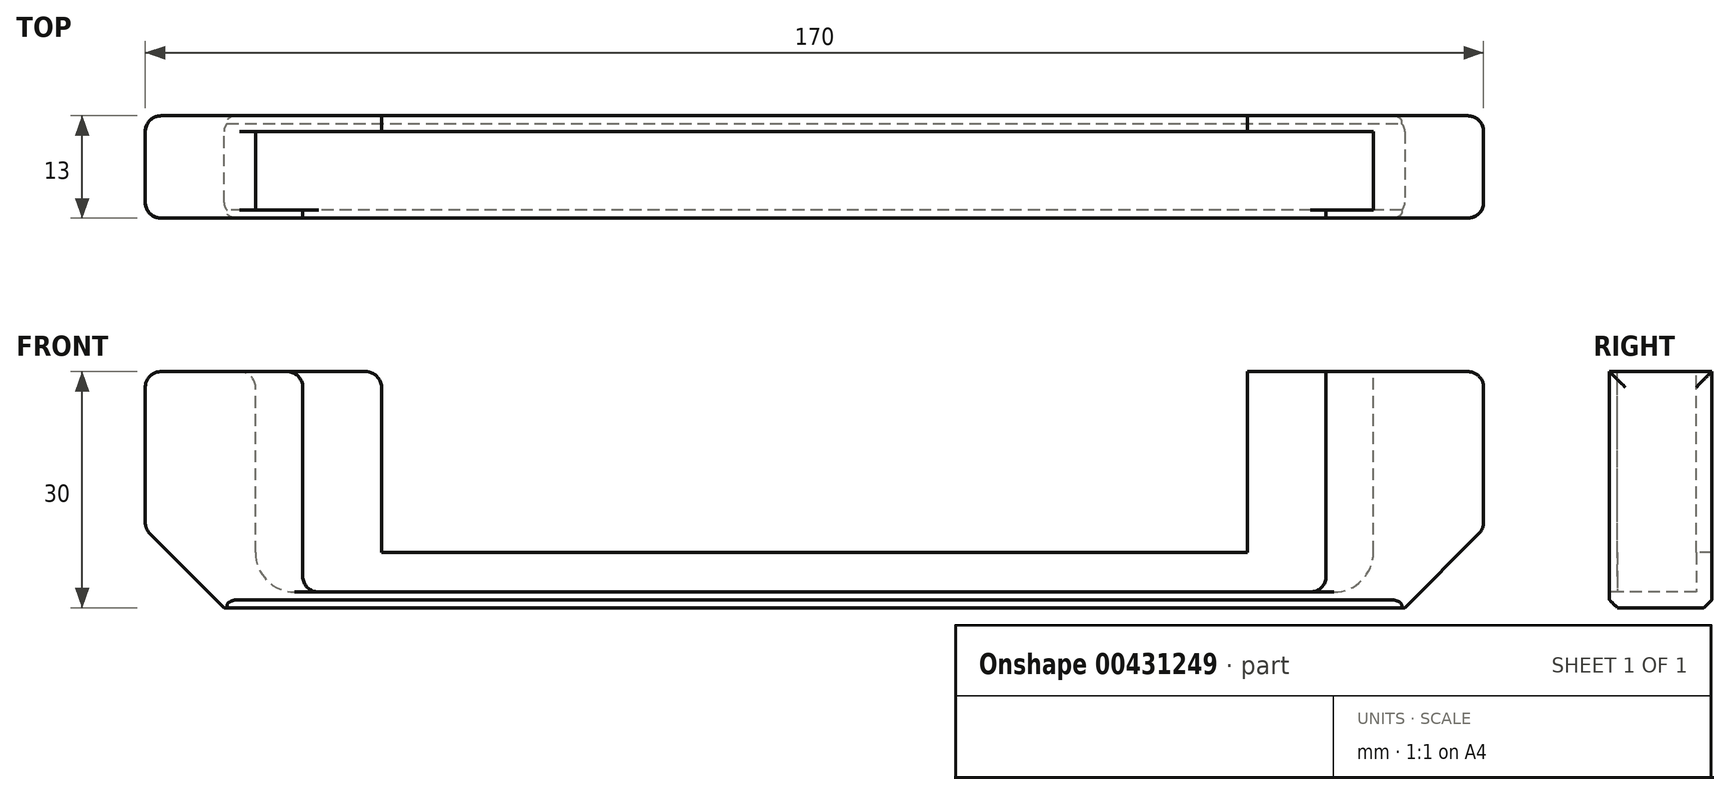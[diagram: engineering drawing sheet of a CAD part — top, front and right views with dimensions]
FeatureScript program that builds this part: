
annotation { "Feature Type Name" : "Feature", "Feature Type Description" : "" }
export const myFeature = defineFeature(function(context is Context, id is Id, definition is map)
    precondition{}
    {
        {
            var Q0;
            Q0=qCreatedBy(makeId("Front.planeOp"),FACE);
            var sketch = newSketch(context, id + "F0", { "sketchPlane" : qUnion([Q0])});
            skLineSegment(sketch, "E0.bottom", {"start": v(-85, 0) * mm, "end": v(85, 0) * mm});
            skLineSegment(sketch, "E0.top", {"start": v(-85, 30) * mm, "end": v(85, 30) * mm});
            skLineSegment(sketch, "E0.left", {"start": v(-85, 0) * mm, "end": v(-85, 30) * mm});
            skLineSegment(sketch, "E0.right", {"start": v(85, 0) * mm, "end": v(85, 30) * mm});
            skSolve(sketch);
        }
        {
            var Q0;
            Q0 = qSketchRegion(id + "F0", true);
            extrude(context, id + "F1", {"entities" : qUnion([Q0]), "depth" : 13 * mm});
        }
        {
            var Q0;
            Q0=makeQuery(id+"F1.opExtrude","SWEPT_FACE",FACE,{"disambiguationData":[OSD([sQuery(id+"F0.wireOp",EDGE,"E0.top")])]});
            var sketch = newSketch(context, id + "F2", { "sketchPlane" : qUnion([Q0])});
            skLineSegment(sketch, "E1.bottom", {"start": v(-71, -2) * mm, "end": v(-55, -2) * mm});
            skLineSegment(sketch, "E1.top", {"start": v(-71, -12) * mm, "end": v(-65, -12) * mm});
            skLineSegment(sketch, "E1.left", {"start": v(-71, -2) * mm, "end": v(-71, -12) * mm});
            skLineSegment(sketch, "E1.right", {"start": v(71, -2) * mm, "end": v(71, -12) * mm});
            skLineSegment(sketch, "E2", {"start": v(-65, -12) * mm, "end": v(-65, -13) * mm});
            skLineSegment(sketch, "E3", {"start": v(-65, -13) * mm, "end": v(65, -13) * mm});
            skLineSegment(sketch, "E4", {"start": v(65, -13) * mm, "end": v(65, -12) * mm});
            skLineSegment(sketch, "E5.trimOffspring", {"start": v(65, -12) * mm, "end": v(71, -12) * mm});
            skLineSegment(sketch, "E6", {"start": v(-55, -2) * mm, "end": v(-55, 0) * mm});
            skLineSegment(sketch, "E7", {"start": v(-55, 0) * mm, "end": v(55, 0) * mm});
            skLineSegment(sketch, "E8", {"start": v(55, 0) * mm, "end": v(55, -2) * mm});
            skLineSegment(sketch, "E9.trimOffspring", {"start": v(55, -2) * mm, "end": v(71, -2) * mm});
            skSolve(sketch);
        }
        {
            var Q0;
            Q0 = qSketchRegion(id + "F2", true);
            extrude(context, id + "F3", {"entities" : qUnion([Q0]), "operationType" : NewBodyOperationType.REMOVE, "oppositeDirection" : true, "depth" : 28 * mm});
        }
        {
            var Q0;
            Q0=makeQuery(id+"F3.boolean.opBoolean","COPY",FACE,{"derivedFrom":makeQuery(id+"F3.opExtrude","CAP_FACE",FACE,{"disambiguationData":[OSD([sQuery(id+"F2.wireOp",EDGE,"E1.bottom"),sQuery(id+"F2.wireOp",EDGE,"E1.top"),sQuery(id+"F2.wireOp",EDGE,"E1.left"),sQuery(id+"F2.wireOp",EDGE,"E1.right"),sQuery(id+"F2.wireOp",EDGE,"E2"),sQuery(id+"F2.wireOp",EDGE,"E3"),sQuery(id+"F2.wireOp",EDGE,"E4"),sQuery(id+"F2.wireOp",EDGE,"E5.trimOffspring"),sQuery(id+"F2.wireOp",EDGE,"E6"),sQuery(id+"F2.wireOp",EDGE,"E7"),sQuery(id+"F2.wireOp",EDGE,"E8"),sQuery(id+"F2.wireOp",EDGE,"E9.trimOffspring")])],"isStart":false})});
            var sketch = newSketch(context, id + "F4", { "sketchPlane" : qUnion([Q0])});
            skLineSegment(sketch, "E10.bottom", {"start": v(55, -2) * mm, "end": v(-55, -2) * mm});
            skLineSegment(sketch, "E10.top", {"start": v(55, 0) * mm, "end": v(-55, 0) * mm});
            skLineSegment(sketch, "E10.left", {"start": v(55, -2) * mm, "end": v(55, 0) * mm});
            skLineSegment(sketch, "E10.right", {"start": v(-55, -2) * mm, "end": v(-55, 0) * mm});
            skSolve(sketch);
        }
        {
            var Q0;
            Q0 = qSketchRegion(id + "F4", true);
            extrude(context, id + "F5", {"entities" : qUnion([Q0]), "operationType" : NewBodyOperationType.ADD, "depth" : 5 * mm});
        }
        {
            var Q0;
            Q0=makeQuery(id+"F1.opExtrude","SWEPT_EDGE",EDGE,{"disambiguationData":[OSD([sQuery(id+"F0.wireOp",EDGE,"E0.bottom"),sQuery(id+"F0.wireOp",EDGE,"E0.right")])]});
            var Q1;
            Q1=makeQuery(id+"F1.opExtrude","SWEPT_EDGE",EDGE,{"disambiguationData":[OSD([sQuery(id+"F0.wireOp",EDGE,"E0.bottom"),sQuery(id+"F0.wireOp",EDGE,"E0.left")])]});
            chamfer(context, id + "F6", {"entities" : qUnion([Q0, Q1]), "width" : 10 * mm, "tangentPropagation" : true});
        }
        {
            var Q0;
            Q0=makeQuery(id+"F3.boolean.opBoolean","COPY",EDGE,{"derivedFrom":makeQuery(id+"F3.opExtrude","CAP_EDGE",EDGE,{"disambiguationData":[OSD([sQuery(id+"F2.wireOp",EDGE,"E1.left")])],"isStart":false})});
            var Q1;
            Q1=makeQuery(id+"F3.boolean.opBoolean","COPY",EDGE,{"derivedFrom":makeQuery(id+"F3.opExtrude","CAP_EDGE",EDGE,{"disambiguationData":[OSD([sQuery(id+"F2.wireOp",EDGE,"E1.right")])],"isStart":false})});
            fillet(context, id + "F7", {"entities" : qUnion([Q0, Q1]), "radius" : 5 * mm, "tangentPropagation" : true, "allowEdgeOverflow" : false});
        }
        {
            var Q0;
            Q0=makeQuery(id+"F1.opExtrude","CAP_EDGE",EDGE,{"disambiguationData":[OSD([sQuery(id+"F0.wireOp",EDGE,"E0.bottom")])],"isStart":false});
            var Q1;
            Q1=makeQuery(id+"F1.opExtrude","CAP_EDGE",EDGE,{"disambiguationData":[OSD([sQuery(id+"F0.wireOp",EDGE,"E0.bottom")])],"isStart":true});
            chamfer(context, id + "F8", {"entities" : qUnion([Q0, Q1]), "width" : 1 * mm, "tangentPropagation" : true});
        }
        {
            var Q0;
            {var subQ0=sQuery(id+"F0.wireOp",EDGE,"E0.left");Q0=makeQuery(id+"F6.opChamfer","BLEND_EDGE",EDGE,{"blendedFrom":[makeQuery(id+"F1.opExtrude","SWEPT_EDGE",EDGE,{"disambiguationData":[OSD([sQuery(id+"F0.wireOp",EDGE,"E0.bottom"),subQ0])]}),makeQuery(id+"F1.opExtrude","SWEPT_FACE",FACE,{"disambiguationData":[OSD([subQ0])]})],"blendedInto":[makeQuery(id+"F1.opExtrude","SWEPT_FACE",FACE,{"disambiguationData":[OSD([subQ0])]})]});}
            var Q1;
            Q1=makeQuery(id+"F1.opExtrude","SWEPT_EDGE",EDGE,{"disambiguationData":[OSD([sQuery(id+"F0.wireOp",EDGE,"E0.top"),sQuery(id+"F0.wireOp",EDGE,"E0.left")])]});
            var Q2;
            Q2=makeQuery(id+"F3.boolean.opBoolean","COPY",EDGE,{"derivedFrom":makeQuery(id+"F3.opExtrude","CAP_EDGE",EDGE,{"disambiguationData":[OSD([sQuery(id+"F2.wireOp",EDGE,"E1.left")])],"isStart":true})});
            var Q3;
            Q3=makeQuery(id+"F3.boolean.opBoolean","COPY",EDGE,{"derivedFrom":makeQuery(id+"F3.opExtrude","CAP_EDGE",EDGE,{"disambiguationData":[OSD([sQuery(id+"F2.wireOp",EDGE,"E1.right")])],"isStart":true})});
            var Q4;
            Q4=makeQuery(id+"F1.opExtrude","SWEPT_EDGE",EDGE,{"disambiguationData":[OSD([sQuery(id+"F0.wireOp",EDGE,"E0.top"),sQuery(id+"F0.wireOp",EDGE,"E0.right")])]});
            var Q5;
            {var subQ0=sQuery(id+"F0.wireOp",EDGE,"E0.right");Q5=makeQuery(id+"F6.opChamfer","BLEND_EDGE",EDGE,{"blendedFrom":[makeQuery(id+"F1.opExtrude","SWEPT_EDGE",EDGE,{"disambiguationData":[OSD([sQuery(id+"F0.wireOp",EDGE,"E0.bottom"),subQ0])]}),makeQuery(id+"F1.opExtrude","SWEPT_FACE",FACE,{"disambiguationData":[OSD([subQ0])]})],"blendedInto":[makeQuery(id+"F1.opExtrude","SWEPT_FACE",FACE,{"disambiguationData":[OSD([subQ0])]})]});}
            var Q6;
            Q6=makeQuery(id+"F5.opExtrude","CAP_EDGE",EDGE,{"disambiguationData":[OSD([sQuery(id+"F4.wireOp",EDGE,"E10.left")])],"isStart":false});
            var Q7;
            Q7=makeQuery(id+"F3.boolean.opBoolean","COPY",EDGE,{"derivedFrom":makeQuery(id+"F3.opExtrude","CAP_EDGE",EDGE,{"disambiguationData":[OSD([sQuery(id+"F2.wireOp",EDGE,"E8")])],"isStart":true})});
            var Q8;
            Q8=makeQuery(id+"F3.boolean.opBoolean","COPY",EDGE,{"derivedFrom":makeQuery(id+"F3.opExtrude","CAP_EDGE",EDGE,{"disambiguationData":[OSD([sQuery(id+"F2.wireOp",EDGE,"E4")])],"isStart":false})});
            var Q9;
            Q9=makeQuery(id+"F3.boolean.opBoolean","COPY",EDGE,{"derivedFrom":makeQuery(id+"F3.opExtrude","CAP_EDGE",EDGE,{"disambiguationData":[OSD([sQuery(id+"F2.wireOp",EDGE,"E4")])],"isStart":true})});
            var Q10;
            Q10=makeQuery(id+"F3.boolean.opBoolean","COPY",EDGE,{"derivedFrom":makeQuery(id+"F3.opExtrude","CAP_EDGE",EDGE,{"disambiguationData":[OSD([sQuery(id+"F2.wireOp",EDGE,"E6")])],"isStart":true})});
            var Q11;
            Q11=makeQuery(id+"F5.opExtrude","CAP_EDGE",EDGE,{"disambiguationData":[OSD([sQuery(id+"F4.wireOp",EDGE,"E10.right")])],"isStart":false});
            var Q12;
            Q12=makeQuery(id+"F3.boolean.opBoolean","COPY",EDGE,{"derivedFrom":makeQuery(id+"F3.opExtrude","CAP_EDGE",EDGE,{"disambiguationData":[OSD([sQuery(id+"F2.wireOp",EDGE,"E2")])],"isStart":false})});
            var Q13;
            Q13=makeQuery(id+"F3.boolean.opBoolean","COPY",EDGE,{"derivedFrom":makeQuery(id+"F3.opExtrude","CAP_EDGE",EDGE,{"disambiguationData":[OSD([sQuery(id+"F2.wireOp",EDGE,"E2")])],"isStart":true})});
            var Q14;
            Q14=makeQuery(id+"F1.opExtrude","CAP_EDGE",EDGE,{"disambiguationData":[OSD([sQuery(id+"F0.wireOp",EDGE,"E0.right")])],"isStart":true});
            var Q15;
            {var subQ0=sQuery(id+"F0.wireOp",EDGE,"E0.right");var subQ1=sQuery(id+"F0.wireOp",EDGE,"E0.bottom");Q15=makeQuery(id+"F6.opChamfer","BLEND_EDGE",EDGE,{"blendedFrom":[makeQuery(id+"F1.opExtrude","SWEPT_EDGE",EDGE,{"disambiguationData":[OSD([subQ1,subQ0])]}),makeQuery(id+"F5.boolean.opBoolean","MERGE",FACE,{"derivedFrom":[makeQuery(id+"F1.opExtrude","CAP_FACE",FACE,{"disambiguationData":[OSD([subQ1,sQuery(id+"F0.wireOp",EDGE,"E0.top"),sQuery(id+"F0.wireOp",EDGE,"E0.left"),subQ0])],"isStart":true}),makeQuery(id+"F5.opExtrude","SWEPT_FACE",FACE,{"disambiguationData":[OSD([sQuery(id+"F4.wireOp",EDGE,"E10.top")])]})]})],"blendedInto":[makeQuery(id+"F5.boolean.opBoolean","MERGE",FACE,{"derivedFrom":[makeQuery(id+"F1.opExtrude","CAP_FACE",FACE,{"disambiguationData":[OSD([subQ1,sQuery(id+"F0.wireOp",EDGE,"E0.top"),sQuery(id+"F0.wireOp",EDGE,"E0.left"),subQ0])],"isStart":true}),makeQuery(id+"F5.opExtrude","SWEPT_FACE",FACE,{"disambiguationData":[OSD([sQuery(id+"F4.wireOp",EDGE,"E10.top")])]})]})]});}
            var Q16;
            {var subQ0=sQuery(id+"F0.wireOp",EDGE,"E0.right");var subQ1=sQuery(id+"F0.wireOp",EDGE,"E0.bottom");Q16=makeQuery(id+"F6.opChamfer","BLEND_EDGE",EDGE,{"blendedFrom":[makeQuery(id+"F1.opExtrude","SWEPT_EDGE",EDGE,{"disambiguationData":[OSD([subQ1,subQ0])]}),makeQuery(id+"F1.opExtrude","CAP_FACE",FACE,{"disambiguationData":[OSD([subQ1,sQuery(id+"F0.wireOp",EDGE,"E0.top"),sQuery(id+"F0.wireOp",EDGE,"E0.left"),subQ0])],"isStart":false})],"blendedInto":[makeQuery(id+"F1.opExtrude","CAP_FACE",FACE,{"disambiguationData":[OSD([subQ1,sQuery(id+"F0.wireOp",EDGE,"E0.top"),sQuery(id+"F0.wireOp",EDGE,"E0.left"),subQ0])],"isStart":false})]});}
            var Q17;
            Q17=makeQuery(id+"F1.opExtrude","CAP_EDGE",EDGE,{"disambiguationData":[OSD([sQuery(id+"F0.wireOp",EDGE,"E0.right")])],"isStart":false});
            var Q18;
            Q18=makeQuery(id+"F1.opExtrude","CAP_EDGE",EDGE,{"disambiguationData":[OSD([sQuery(id+"F0.wireOp",EDGE,"E0.left")])],"isStart":true});
            var Q19;
            {var subQ0=sQuery(id+"F0.wireOp",EDGE,"E0.left");var subQ1=sQuery(id+"F0.wireOp",EDGE,"E0.bottom");Q19=makeQuery(id+"F6.opChamfer","BLEND_EDGE",EDGE,{"blendedFrom":[makeQuery(id+"F1.opExtrude","SWEPT_EDGE",EDGE,{"disambiguationData":[OSD([subQ1,subQ0])]}),makeQuery(id+"F5.boolean.opBoolean","MERGE",FACE,{"derivedFrom":[makeQuery(id+"F1.opExtrude","CAP_FACE",FACE,{"disambiguationData":[OSD([subQ1,sQuery(id+"F0.wireOp",EDGE,"E0.top"),subQ0,sQuery(id+"F0.wireOp",EDGE,"E0.right")])],"isStart":true}),makeQuery(id+"F5.opExtrude","SWEPT_FACE",FACE,{"disambiguationData":[OSD([sQuery(id+"F4.wireOp",EDGE,"E10.top")])]})]})],"blendedInto":[makeQuery(id+"F5.boolean.opBoolean","MERGE",FACE,{"derivedFrom":[makeQuery(id+"F1.opExtrude","CAP_FACE",FACE,{"disambiguationData":[OSD([subQ1,sQuery(id+"F0.wireOp",EDGE,"E0.top"),subQ0,sQuery(id+"F0.wireOp",EDGE,"E0.right")])],"isStart":true}),makeQuery(id+"F5.opExtrude","SWEPT_FACE",FACE,{"disambiguationData":[OSD([sQuery(id+"F4.wireOp",EDGE,"E10.top")])]})]})]});}
            var Q20;
            Q20=makeQuery(id+"F1.opExtrude","CAP_EDGE",EDGE,{"disambiguationData":[OSD([sQuery(id+"F0.wireOp",EDGE,"E0.left")])],"isStart":false});
            var Q21;
            {var subQ0=sQuery(id+"F0.wireOp",EDGE,"E0.left");var subQ1=sQuery(id+"F0.wireOp",EDGE,"E0.bottom");Q21=makeQuery(id+"F6.opChamfer","BLEND_EDGE",EDGE,{"blendedFrom":[makeQuery(id+"F1.opExtrude","SWEPT_EDGE",EDGE,{"disambiguationData":[OSD([subQ1,subQ0])]}),makeQuery(id+"F1.opExtrude","CAP_FACE",FACE,{"disambiguationData":[OSD([subQ1,sQuery(id+"F0.wireOp",EDGE,"E0.top"),subQ0,sQuery(id+"F0.wireOp",EDGE,"E0.right")])],"isStart":false})],"blendedInto":[makeQuery(id+"F1.opExtrude","CAP_FACE",FACE,{"disambiguationData":[OSD([subQ1,sQuery(id+"F0.wireOp",EDGE,"E0.top"),subQ0,sQuery(id+"F0.wireOp",EDGE,"E0.right")])],"isStart":false})]});}
            fillet(context, id + "F9", {"entities" : qUnion([Q0, Q1, Q2, Q3, Q4, Q5, Q6, Q7, Q8, Q9, Q10, Q11, Q12, Q13, Q14, Q15, Q16, Q17, Q18, Q19, Q20, Q21]), "radius" : 2 * mm, "tangentPropagation" : true, "allowEdgeOverflow" : false});
        }
    });
